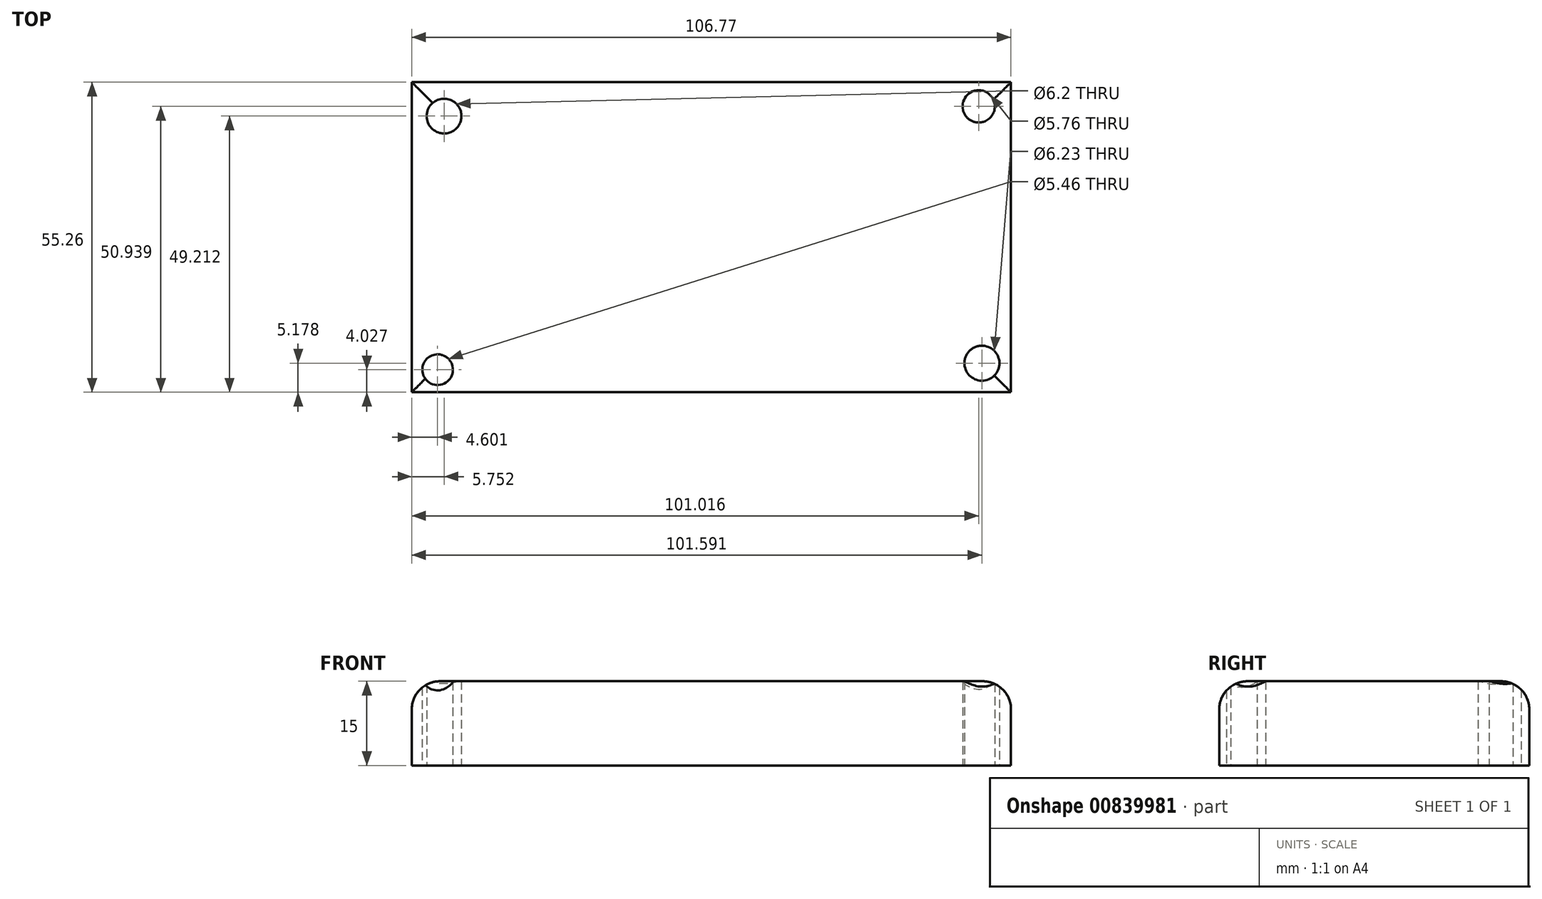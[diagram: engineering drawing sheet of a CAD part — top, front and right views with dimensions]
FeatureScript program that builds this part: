
annotation { "Feature Type Name" : "Feature", "Feature Type Description" : "" }
export const myFeature = defineFeature(function(context is Context, id is Id, definition is map)
    precondition{}
    {
        {
            var Q0;
            Q0=qCreatedBy(makeId("Top.planeOp"),FACE);
            var sketch = newSketch(context, id + "F0", { "sketchPlane" : qUnion([Q0])});
            skLineSegment(sketch, "E0.bottom", {"start": v(-47.34, 35.26) * mm, "end": v(59.43, 35.26) * mm});
            skLineSegment(sketch, "E0.top", {"start": v(-47.34, -20) * mm, "end": v(59.43, -20) * mm});
            skLineSegment(sketch, "E0.left", {"start": v(-47.34, 35.26) * mm, "end": v(-47.34, -20) * mm});
            skLineSegment(sketch, "E0.right", {"start": v(59.43, 35.26) * mm, "end": v(59.43, -20) * mm});
            skCircle(sketch, "E1", {"center": v(-41.59, 29.21) * mm, "radius": 3.1 * mm});
            skCircle(sketch, "E2", {"center": v(53.68, 30.94) * mm, "radius": 2.88 * mm});
            skCircle(sketch, "E3", {"center": v(54.25, -14.82) * mm, "radius": 3.11 * mm});
            skCircle(sketch, "E4", {"center": v(-42.74, -15.97) * mm, "radius": 2.73 * mm});
            skSolve(sketch);
        }
        {
            var Q0;
            Q0=makeQuery(id+"F0.imprint","IMPRINT",FACE,{"disambiguationData":[TD([[makeQuery(id+"F0.imprint","IMPRINT",EDGE,{"derivedFrom":sQuery(id+"F0.wireOp",EDGE,"E0.bottom")}),-1.0]])]});
            extrude(context, id + "F1", {"entities" : qUnion([Q0]), "depth" : 15 * mm, "offsetDistance" : 25 * mm});
        }
        {
            var Q0;
            Q0=makeQuery(id+"F1.opExtrude","CAP_EDGE",EDGE,{"disambiguationData":[OSD([sQuery(id+"F0.wireOp",EDGE,"E0.top")])],"isStart":false});
            var Q1;
            Q1=makeQuery(id+"F1.opExtrude","CAP_EDGE",EDGE,{"disambiguationData":[OSD([sQuery(id+"F0.wireOp",EDGE,"E0.right")])],"isStart":false});
            var Q2;
            Q2=makeQuery(id+"F1.opExtrude","CAP_EDGE",EDGE,{"disambiguationData":[OSD([sQuery(id+"F0.wireOp",EDGE,"E0.bottom")])],"isStart":false});
            var Q3;
            Q3=makeQuery(id+"F1.opExtrude","CAP_EDGE",EDGE,{"disambiguationData":[OSD([sQuery(id+"F0.wireOp",EDGE,"E0.left")])],"isStart":false});
            fillet(context, id + "F2", {"entities" : qUnion([Q0, Q1, Q2, Q3]), "radius" : 5 * mm, "tangentPropagation" : true, "allowEdgeOverflow" : false});
        }
    });
